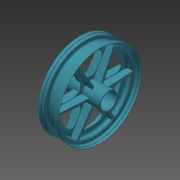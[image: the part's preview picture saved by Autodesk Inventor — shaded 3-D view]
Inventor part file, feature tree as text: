
AUTODESK INVENTOR PART (.ipt)
format: ipt  version: 2015 (Build 190159000, 159)  size: 621,056 bytes
history: native  units: mm
features: other x7, sketch x5, extrude x2, revolve x1, hole x1, loft x1, pattern_circular x1
ambient origin geometry x8: Origin, YZ Plane, XZ Plane, XY Plane, X Axis, Y Axis, Z Axis, Center Point
bodies: Body1 (feature_tree)
feature tree (18):
  other  "Bryła1"
  revolve  "Obrót1"
  hole  "Otwór na oś"  [1 undecoded]
  extrude  "Wyciągnięcie zmniejszenie masy"  TaperAngle=60.0deg  [1 undecoded]
  other  "Płaszczyzna konstrukcyjna1"
  sketch  "Szkic6"
  loft  "Wyciągnięcie wzmocnienie"
  extrude  "Wyciągnięcie proste2"  Depth=2.5mm
  pattern_circular  "Szyk wzmocnień"  [2 undecoded]
  sketch  "Szkic1"
  sketch  "Szkic5"
  sketch  "Szkic8"
  sketch  "Szkic9"
  other  "Płaszczyzna konstrukcyjna3"
  other  "Płaszczyzna konstrukcyjna4"
  other  "Płaszczyzna konstrukcyjna5"
  other  "Płaszczyzna konstrukcyjna6"
  other  "Płaszczyzna konstrukcyjna7"
note: 4 required parameter values undecoded (feature->parameter linkage not recoverable at this tier; creation-order binding heuristic only, values carry confidence <= 0.55)
